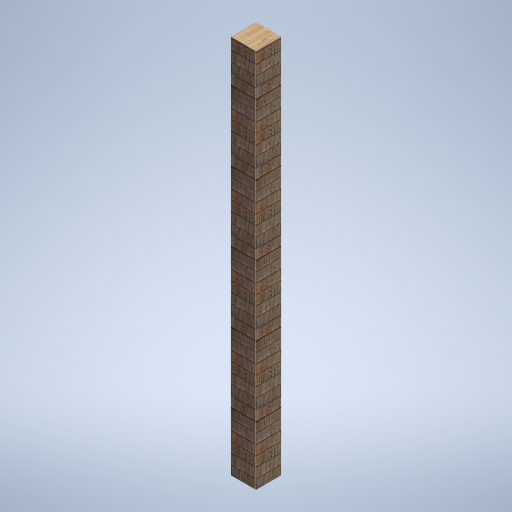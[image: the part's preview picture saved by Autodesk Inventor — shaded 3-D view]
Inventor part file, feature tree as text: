
AUTODESK INVENTOR PART (.ipt)
format: ipt  version: 2024.2 (Build 282272000, 272)  size: 312,832 bytes
history: native  units: in
note: dims shown in document units (in); Inventor stores cm internally (conversion verified against a paired STEP export)
features: other x3, sketch x1
ambient origin geometry x8: Origin, YZ Plane, XZ Plane, XY Plane, X Axis, Y Axis, Z Axis, Center Point
bodies: Solid1 (feature_tree)
feature tree (4):
  other  "support_frame_03_MIR.ipt"
  other  "Solid1::support_frame_03_MIR.ipt"
  other  "TaggingFeature1"
  sketch  "Sketch1"  dims[d0=0.3937in]
